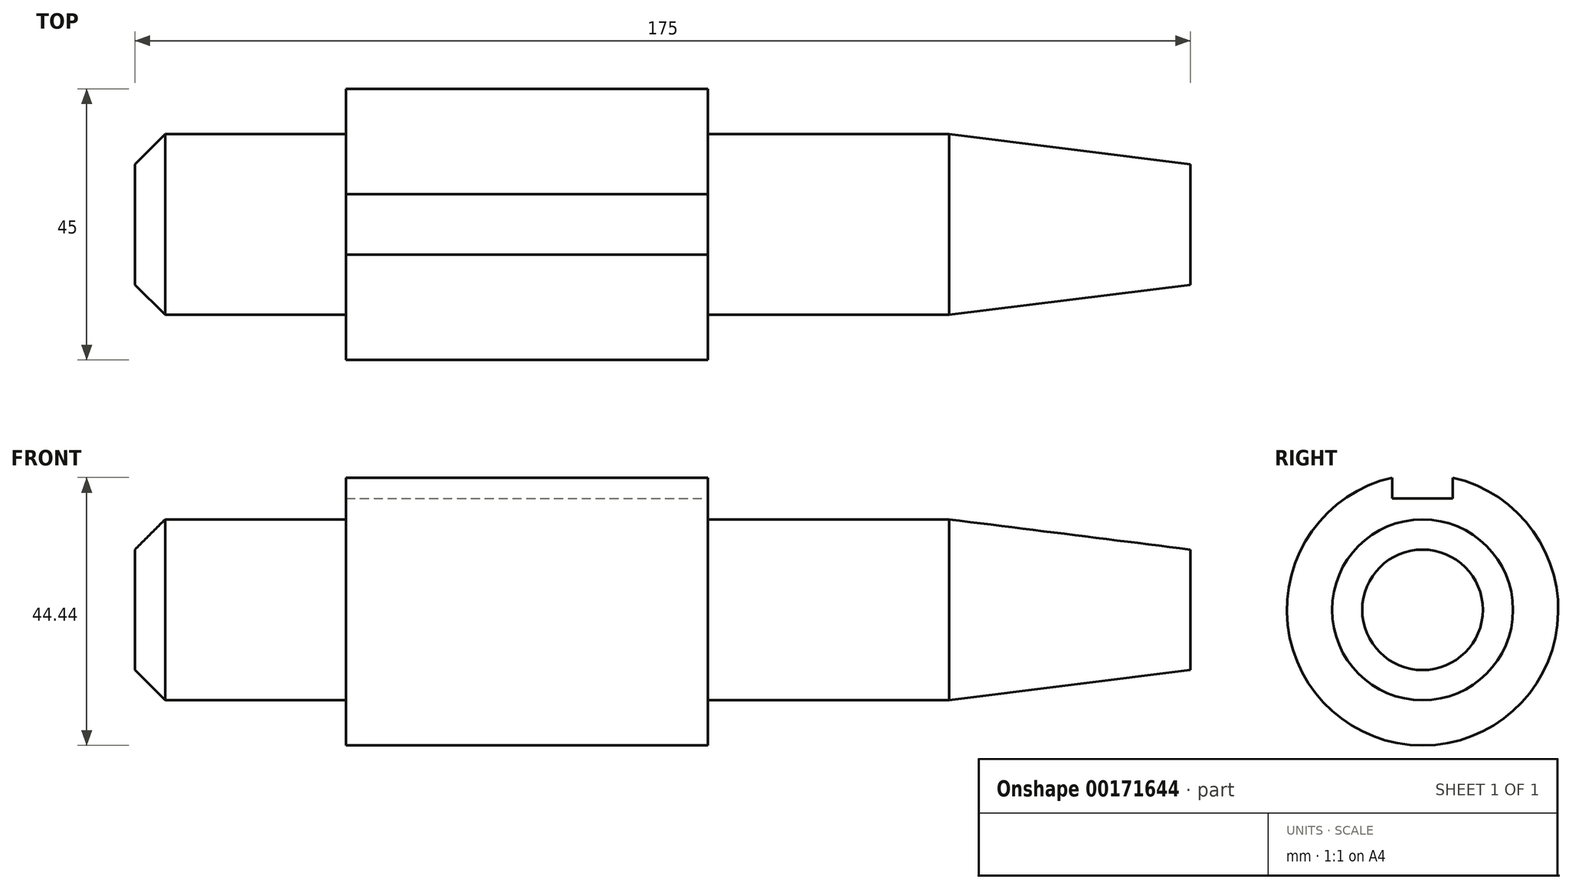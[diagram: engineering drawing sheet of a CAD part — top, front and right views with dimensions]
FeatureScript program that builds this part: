
annotation { "Feature Type Name" : "Feature", "Feature Type Description" : "" }
export const myFeature = defineFeature(function(context is Context, id is Id, definition is map)
    precondition{}
    {
        {
            var Q0;
            Q0=qCreatedBy(makeId("Front.planeOp"),FACE);
            var sketch = newSketch(context, id + "F0", { "sketchPlane" : qUnion([Q0])});
            skLineSegment(sketch, "E0", {"start": v(0, 0) * mm, "end": v(0, 15) * mm});
            skLineSegment(sketch, "E1", {"start": v(0, 15) * mm, "end": v(35, 15) * mm});
            skLineSegment(sketch, "E2", {"start": v(35, 15) * mm, "end": v(35, 22.5) * mm});
            skLineSegment(sketch, "E3", {"start": v(35, 22.5) * mm, "end": v(95, 22.5) * mm});
            skLineSegment(sketch, "E4", {"start": v(95, 22.5) * mm, "end": v(95, 15) * mm});
            skLineSegment(sketch, "E5", {"start": v(95, 15) * mm, "end": v(135, 15) * mm});
            skLineSegment(sketch, "E6", {"start": v(135, 15) * mm, "end": v(175, 10) * mm});
            skLineSegment(sketch, "E7", {"start": v(175, 10) * mm, "end": v(175, 0) * mm});
            skLineSegment(sketch, "E8", {"start": v(175, 0) * mm, "end": v(0, 0) * mm});
            skSolve(sketch);
        }
        {
            var Q0;
            Q0=qCreatedBy(makeId("Front.planeOp"),FACE);
            var sketch = newSketch(context, id + "F1", { "sketchPlane" : qUnion([Q0])});
            skLineSegment(sketch, "E9", {"start": v(0, 0) * mm, "end": v(219.18, 0) * mm, "construction": true});
            skSolve(sketch);
        }
        {
            var Q0;
            Q0=makeQuery(id+"F0.imprint","IMPRINT",FACE,{"disambiguationData":[TD([[makeQuery(id+"F0.imprint","IMPRINT",EDGE,{"derivedFrom":sQuery(id+"F0.wireOp",EDGE,"E0")}),-1.0]])]});
            var Q1;
            Q1=sQuery(id+"F1.wireOp",EDGE,"E9");
            revolve(context, id + "F2", {"entities" : qUnion([Q0]), "axis" : qUnion([Q1]), "revolveType" : RevolveType.FULL});
        }
        {
            var Q0;
            Q0=makeQuery(id+"F2.opRevolve","SWEPT_FACE",FACE,{"disambiguationData":[OSD([sQuery(id+"F0.wireOp",EDGE,"E4")])]});
            var sketch = newSketch(context, id + "F3", { "sketchPlane" : qUnion([Q0])});
            skLineSegment(sketch, "E10.bottom", {"start": v(-5, 22.5) * mm, "end": v(5, 22.5) * mm});
            skLineSegment(sketch, "E10.top", {"start": v(-5, 18.5) * mm, "end": v(5, 18.5) * mm});
            skLineSegment(sketch, "E10.left", {"start": v(-5, 22.5) * mm, "end": v(-5, 18.5) * mm});
            skLineSegment(sketch, "E10.right", {"start": v(5, 22.5) * mm, "end": v(5, 18.5) * mm});
            skSolve(sketch);
        }
        {
            var Q0;
            {var subQ1=sQuery(id+"F3.wireOp",EDGE,"E10.top");Q0=makeQuery(id+"F3.imprint","IMPRINT",FACE,{"disambiguationData":[TD([[makeQuery(id+"F3.imprint","IMPRINT",EDGE,{"derivedFrom":subQ1}),1.0]])]});}
            extrude(context, id + "F4", {"entities" : qUnion([Q0]), "operationType" : NewBodyOperationType.REMOVE, "endBound" : BoundingType.UP_TO_NEXT, "oppositeDirection" : true, "depth" : 25 * mm});
        }
        {
            var Q0;
            Q0=qCreatedBy(makeId("Front.planeOp"),FACE);
            var sketch = newSketch(context, id + "F5", { "sketchPlane" : qUnion([Q0])});
            skLineSegment(sketch, "E11", {"start": v(0, 15) * mm, "end": v(0, 10) * mm});
            skLineSegment(sketch, "E12", {"start": v(0, 10) * mm, "end": v(5, 15) * mm});
            skLineSegment(sketch, "E13", {"start": v(5, 15) * mm, "end": v(0, 15) * mm});
            skSolve(sketch);
        }
        {
            var Q0;
            Q0 = qSketchRegion(id + "F5", true);
            var Q1;
            Q1=sQuery(id+"F1.wireOp",EDGE,"E9");
            revolve(context, id + "F6", {"operationType" : NewBodyOperationType.REMOVE, "entities" : qUnion([Q0]), "axis" : qUnion([Q1]), "revolveType" : RevolveType.FULL});
        }
    });
